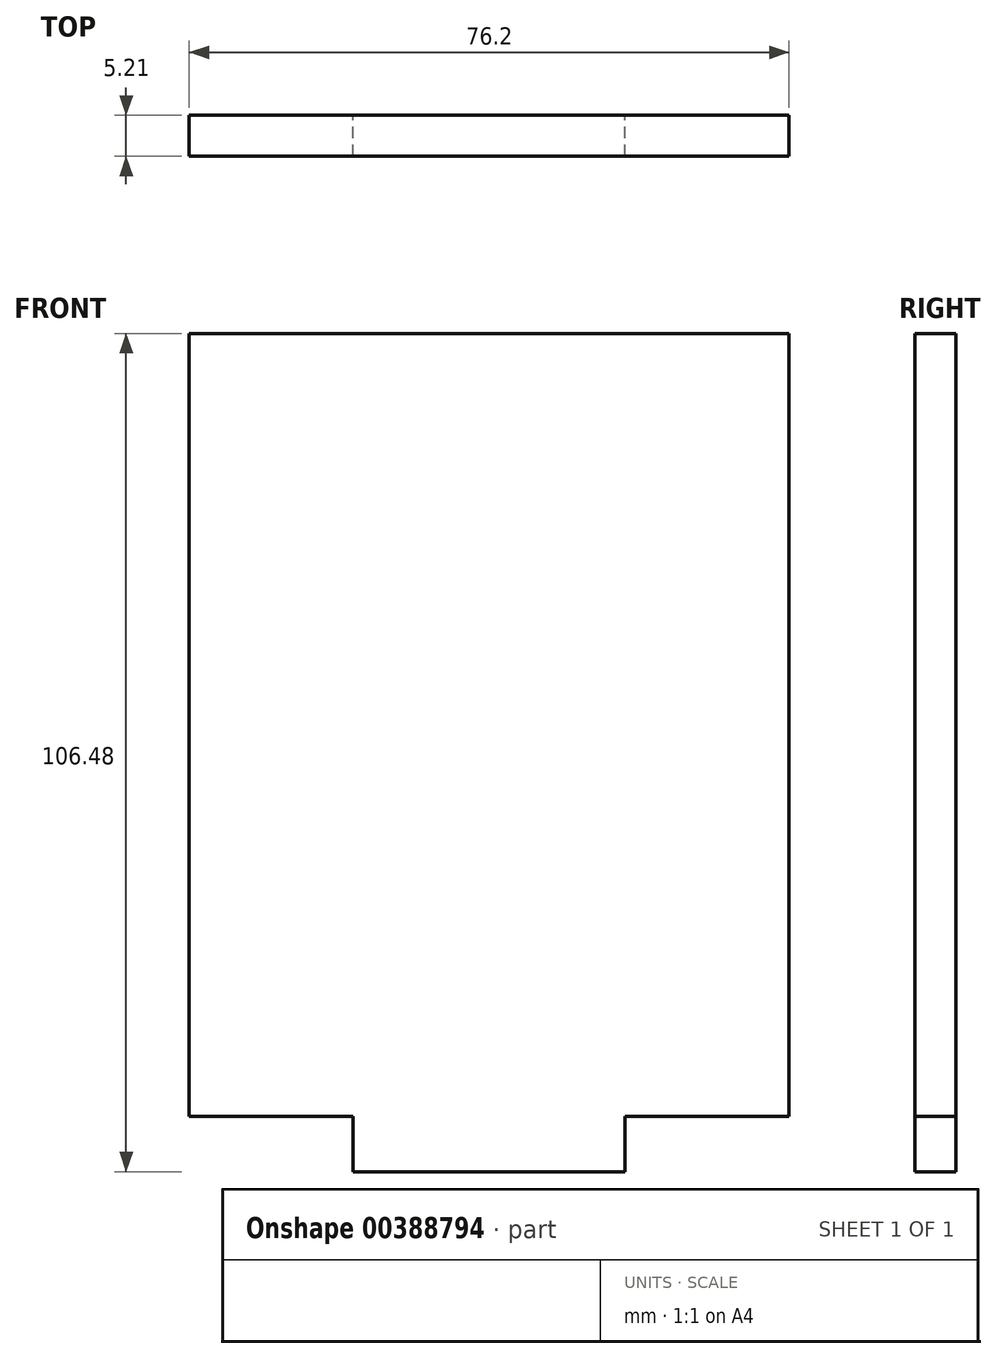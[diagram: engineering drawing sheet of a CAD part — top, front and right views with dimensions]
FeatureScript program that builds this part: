
annotation { "Feature Type Name" : "Feature", "Feature Type Description" : "" }
export const myFeature = defineFeature(function(context is Context, id is Id, definition is map)
    precondition{}
    {
        {
            var Q0;
            Q0=qCreatedBy(makeId("Front.planeOp"),FACE);
            var sketch = newSketch(context, id + "F0", { "sketchPlane" : qUnion([Q0])});
            skLineSegment(sketch, "E0.bottom", {"start": v(38.1, -53.24) * mm, "end": v(-38.1, -53.24) * mm});
            skLineSegment(sketch, "E0.top", {"start": v(38.1, 53.24) * mm, "end": v(-38.1, 53.24) * mm});
            skLineSegment(sketch, "E0.left", {"start": v(38.1, -53.24) * mm, "end": v(38.1, 53.24) * mm});
            skLineSegment(sketch, "E0.right", {"start": v(-38.1, -53.24) * mm, "end": v(-38.1, 53.24) * mm});
            skPoint(sketch, "E0.middle", {"position": v(0, 0) * mm});
            skSolve(sketch);
        }
        {
            var Q0;
            Q0=makeQuery(id+"F0.imprint","IMPRINT",FACE,{"disambiguationData":[TD([[makeQuery(id+"F0.imprint","IMPRINT",EDGE,{"derivedFrom":sQuery(id+"F0.wireOp",EDGE,"E0.bottom")}),-1.0]])]});
            extrude(context, id + "F1", {"entities" : qUnion([Q0]), "depth" : 5.2 * mm});
        }
        {
            var Q0;
            Q0=makeQuery(id+"F1.opExtrude","CAP_FACE",FACE,{"disambiguationData":[OSD([sQuery(id+"F0.wireOp",EDGE,"E0.bottom"),sQuery(id+"F0.wireOp",EDGE,"E0.top"),sQuery(id+"F0.wireOp",EDGE,"E0.left"),sQuery(id+"F0.wireOp",EDGE,"E0.right")])],"isStart":true});
            var sketch = newSketch(context, id + "F2", { "sketchPlane" : qUnion([Q0])});
            skLineSegment(sketch, "E1.bottom", {"start": v(38.1, -53.24) * mm, "end": v(17.27, -53.24) * mm});
            skLineSegment(sketch, "E1.top", {"start": v(38.1, -46.2) * mm, "end": v(17.27, -46.2) * mm});
            skLineSegment(sketch, "E1.left", {"start": v(38.1, -53.24) * mm, "end": v(38.1, -46.2) * mm});
            skLineSegment(sketch, "E1.right", {"start": v(17.27, -53.24) * mm, "end": v(17.27, -46.2) * mm});
            skLineSegment(sketch, "E2.bottom", {"start": v(-38.1, -53.24) * mm, "end": v(-17.27, -53.24) * mm});
            skLineSegment(sketch, "E2.top", {"start": v(-38.1, -46.2) * mm, "end": v(-17.27, -46.2) * mm});
            skLineSegment(sketch, "E2.left", {"start": v(-38.1, -53.24) * mm, "end": v(-38.1, -46.2) * mm});
            skLineSegment(sketch, "E2.right", {"start": v(-17.27, -53.24) * mm, "end": v(-17.27, -46.2) * mm});
            skSolve(sketch);
        }
        {
            var Q0;
            Q0 = qSketchRegion(id + "F2", true);
            extrude(context, id + "F3", {"entities" : qUnion([Q0]), "operationType" : NewBodyOperationType.REMOVE, "endBound" : BoundingType.UP_TO_NEXT, "oppositeDirection" : true, "depth" : 25.4 * mm});
        }
    });
